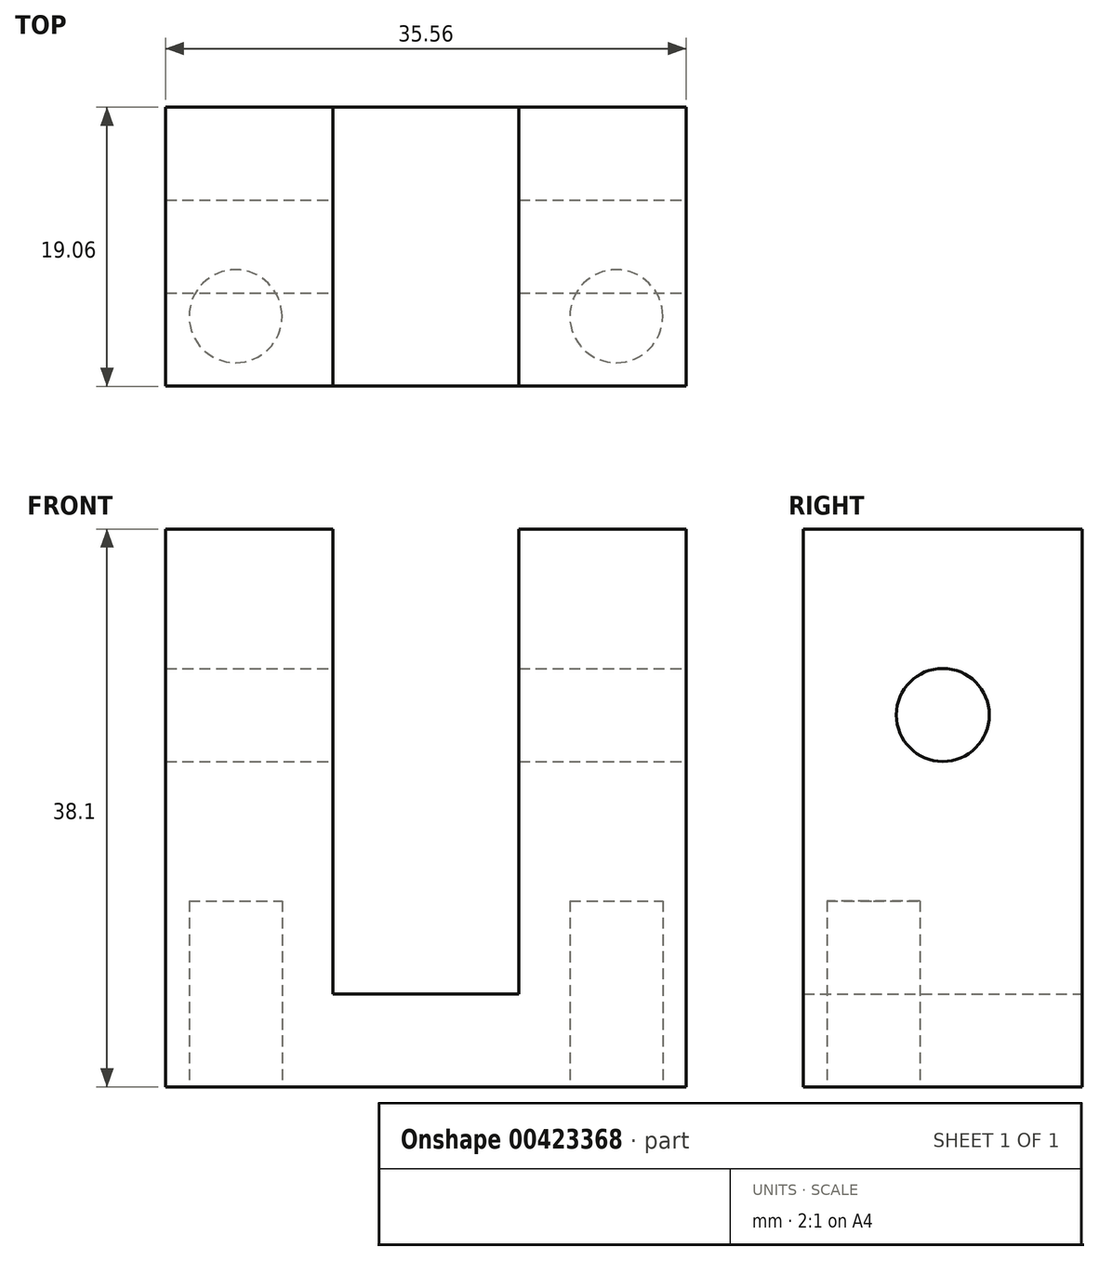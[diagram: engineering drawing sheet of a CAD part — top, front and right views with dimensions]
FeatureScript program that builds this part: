
annotation { "Feature Type Name" : "Feature", "Feature Type Description" : "" }
export const myFeature = defineFeature(function(context is Context, id is Id, definition is map)
    precondition{}
    {
        {
            var Q0;
            Q0=qCreatedBy(makeId("Front.planeOp"),FACE);
            var sketch = newSketch(context, id + "F0", { "sketchPlane" : qUnion([Q0])});
            skLineSegment(sketch, "E0.bottom", {"start": v(-17.78, 0) * mm, "end": v(17.78, 0) * mm});
            skLineSegment(sketch, "E0.top", {"start": v(-17.78, 38.1) * mm, "end": v(17.78, 38.1) * mm});
            skLineSegment(sketch, "E0.left", {"start": v(-17.78, 0) * mm, "end": v(-17.78, 38.1) * mm});
            skLineSegment(sketch, "E0.right", {"start": v(17.78, 0) * mm, "end": v(17.78, 38.1) * mm});
            skLineSegment(sketch, "E1.bottom", {"start": v(6.35, 38.1) * mm, "end": v(-6.35, 38.1) * mm});
            skLineSegment(sketch, "E1.top", {"start": v(6.35, 6.35) * mm, "end": v(-6.35, 6.35) * mm});
            skLineSegment(sketch, "E1.left", {"start": v(6.35, 38.1) * mm, "end": v(6.35, 6.35) * mm});
            skLineSegment(sketch, "E1.right", {"start": v(-6.35, 38.1) * mm, "end": v(-6.35, 6.35) * mm});
            skSolve(sketch);
        }
        {
            var Q0;
            Q0=makeQuery(id+"F0.imprint","IMPRINT",FACE,{"disambiguationData":[TD([[makeQuery(id+"F0.imprint","IMPRINT",EDGE,{"derivedFrom":sQuery(id+"F0.wireOp",EDGE,"E0.bottom")}),1.0]])]});
            extrude(context, id + "F1", {"entities" : qUnion([Q0]), "endBound" : BoundingType.SYMMETRIC, "depth" : 19.05 * mm});
        }
        {
            var Q0;
            Q0=makeQuery(id+"F1.opExtrude","SWEPT_FACE",FACE,{"disambiguationData":[OSD([sQuery(id+"F0.wireOp",EDGE,"E0.right")])]});
            var sketch = newSketch(context, id + "F2", { "sketchPlane" : qUnion([Q0])});
            skCircle(sketch, "E2", {"center": v(0, 25.4) * mm, "radius": 3.18 * mm});
            skSolve(sketch);
        }
        {
            var Q0;
            Q0 = qSketchRegion(id + "F2", true);
            extrude(context, id + "F3", {"entities" : qUnion([Q0]), "operationType" : NewBodyOperationType.REMOVE, "endBound" : BoundingType.THROUGH_ALL, "oppositeDirection" : true, "depth" : 25.4 * mm});
        }
        {
            var Q0;
            Q0=makeQuery(id+"F1.opExtrude","SWEPT_FACE",FACE,{"disambiguationData":[OSD([sQuery(id+"F0.wireOp",EDGE,"E0.bottom")])]});
            var sketch = newSketch(context, id + "F4", { "sketchPlane" : qUnion([Q0])});
            skCircle(sketch, "E3", {"center": v(-13, 4.75) * mm, "radius": 3.18 * mm});
            skCircle(sketch, "E4", {"center": v(13, 4.75) * mm, "radius": 3.18 * mm});
            skSolve(sketch);
        }
        {
            var Q0;
            Q0 = qSketchRegion(id + "F4", true);
            extrude(context, id + "F5", {"entities" : qUnion([Q0]), "operationType" : NewBodyOperationType.REMOVE, "oppositeDirection" : true, "depth" : 12.7 * mm});
        }
    });
